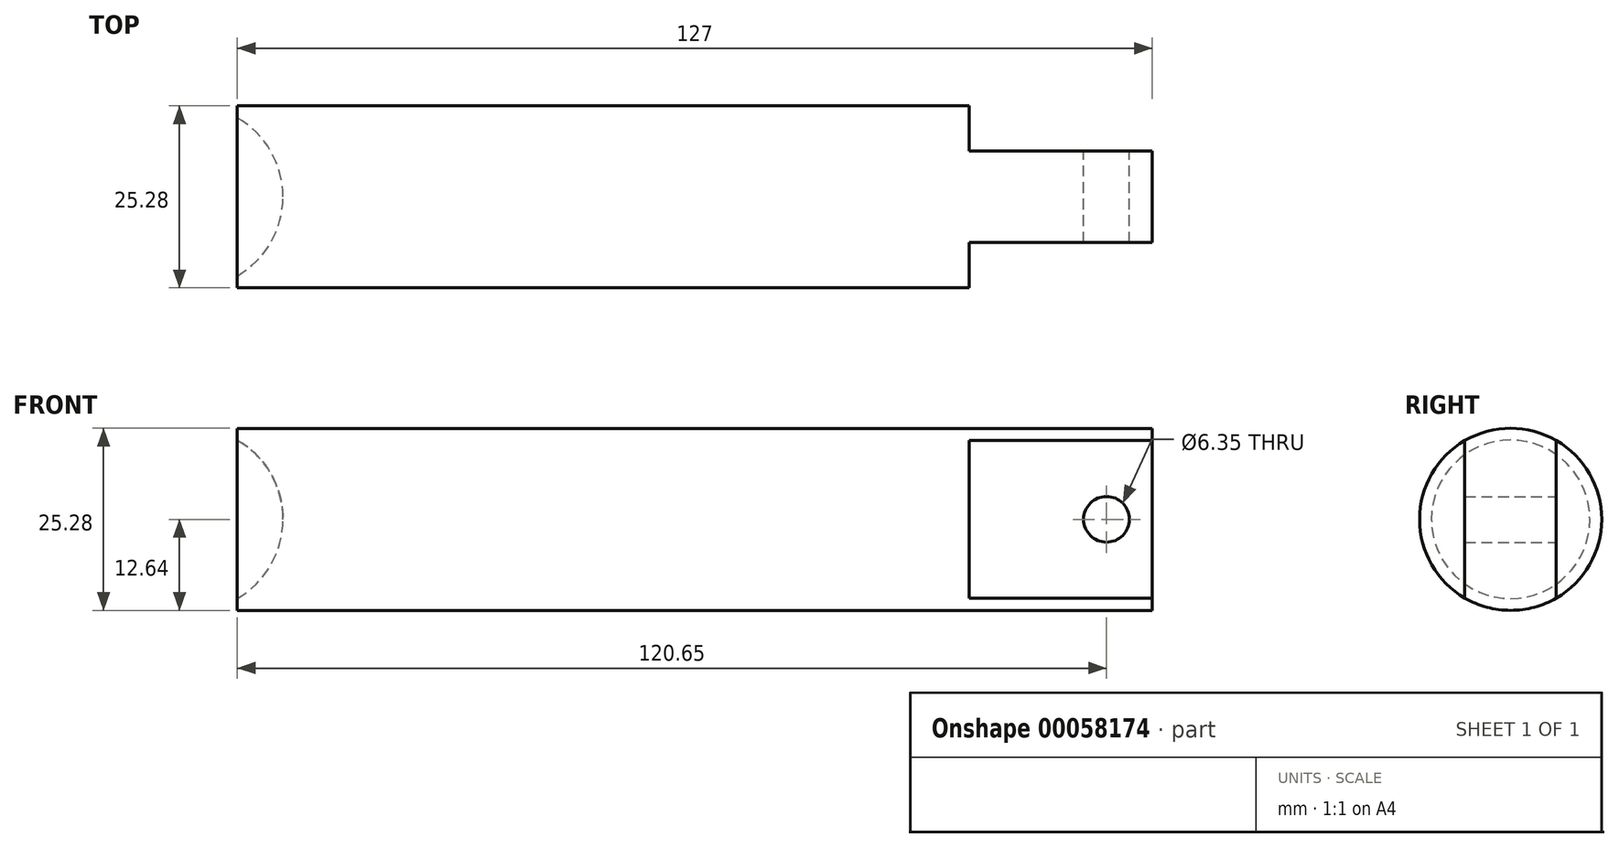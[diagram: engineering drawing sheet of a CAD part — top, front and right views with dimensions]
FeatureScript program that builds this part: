
annotation { "Feature Type Name" : "Feature", "Feature Type Description" : "" }
export const myFeature = defineFeature(function(context is Context, id is Id, definition is map)
    precondition{}
    {
        {
            var Q0;
            Q0=qCreatedBy(makeId("Front.planeOp"),FACE);
            var sketch = newSketch(context, id + "F0", { "sketchPlane" : qUnion([Q0])});
            skLineSegment(sketch, "E0", {"start": v(0, 11) * mm, "end": v(0, 12.64) * mm});
            skLineSegment(sketch, "E1", {"start": v(0, 12.64) * mm, "end": v(127, 12.64) * mm});
            skLineSegment(sketch, "E2", {"start": v(127, 12.64) * mm, "end": v(127, 0) * mm});
            skLineSegment(sketch, "E3", {"start": v(127, 0) * mm, "end": v(6.35, 0) * mm});
            skArc(sketch, "E4", {"start": v(6.35, 0) * mm, "mid": v(4.65, 6.35) * mm, "end": v(0, 11) * mm});
            skSolve(sketch);
        }
        {
            var Q0;
            Q0 = qSketchRegion(id + "F0", true);
            var Q1;
            Q1=sQuery(id+"F0.wireOp",EDGE,"E3");
            revolve(context, id + "F1", {"entities" : qUnion([Q0]), "axis" : qUnion([Q1]), "revolveType" : RevolveType.FULL});
        }
        {
            var Q0;
            Q0=makeQuery(id+"F1.opRevolve","SWEPT_FACE",FACE,{"disambiguationData":[OSD([sQuery(id+"F0.wireOp",EDGE,"E2")])]});
            var sketch = newSketch(context, id + "F2", { "sketchPlane" : qUnion([Q0])});
            skLineSegment(sketch, "E5.bottom", {"start": v(-21.85, 14.8) * mm, "end": v(-6.35, 14.8) * mm});
            skLineSegment(sketch, "E5.top", {"start": v(-21.85, -22.36) * mm, "end": v(-6.35, -22.36) * mm});
            skLineSegment(sketch, "E5.left", {"start": v(-21.85, 14.8) * mm, "end": v(-21.85, -22.36) * mm});
            skLineSegment(sketch, "E5.right", {"start": v(-6.35, 14.8) * mm, "end": v(-6.35, -22.36) * mm});
            skLineSegment(sketch, "E6.bottom", {"start": v(21.3, 18.73) * mm, "end": v(6.35, 18.73) * mm});
            skLineSegment(sketch, "E6.top", {"start": v(21.3, -26.28) * mm, "end": v(6.35, -26.28) * mm});
            skLineSegment(sketch, "E6.left", {"start": v(21.3, 18.73) * mm, "end": v(21.3, -26.28) * mm});
            skLineSegment(sketch, "E6.right", {"start": v(6.35, 18.73) * mm, "end": v(6.35, -26.28) * mm});
            skSolve(sketch);
        }
        {
            var Q0;
            Q0 = qSketchRegion(id + "F2", true);
            extrude(context, id + "F3", {"entities" : qUnion([Q0]), "operationType" : NewBodyOperationType.REMOVE, "oppositeDirection" : true, "depth" : 25.4 * mm});
        }
        {
            var Q0;
            Q0=makeQuery(id+"F3.boolean.opBoolean","COPY",FACE,{"derivedFrom":makeQuery(id+"F3.opExtrude","SWEPT_FACE",FACE,{"disambiguationData":[OSD([sQuery(id+"F2.wireOp",EDGE,"E6.right")])]})});
            var sketch = newSketch(context, id + "F4", { "sketchPlane" : qUnion([Q0])});
            skCircle(sketch, "E7", {"center": v(-120.65, 0) * mm, "radius": 3.18 * mm});
            skSolve(sketch);
        }
        {
            var Q0;
            Q0 = qSketchRegion(id + "F4", true);
            extrude(context, id + "F5", {"entities" : qUnion([Q0]), "operationType" : NewBodyOperationType.REMOVE, "oppositeDirection" : true, "depth" : 25.4 * mm});
        }
    });
